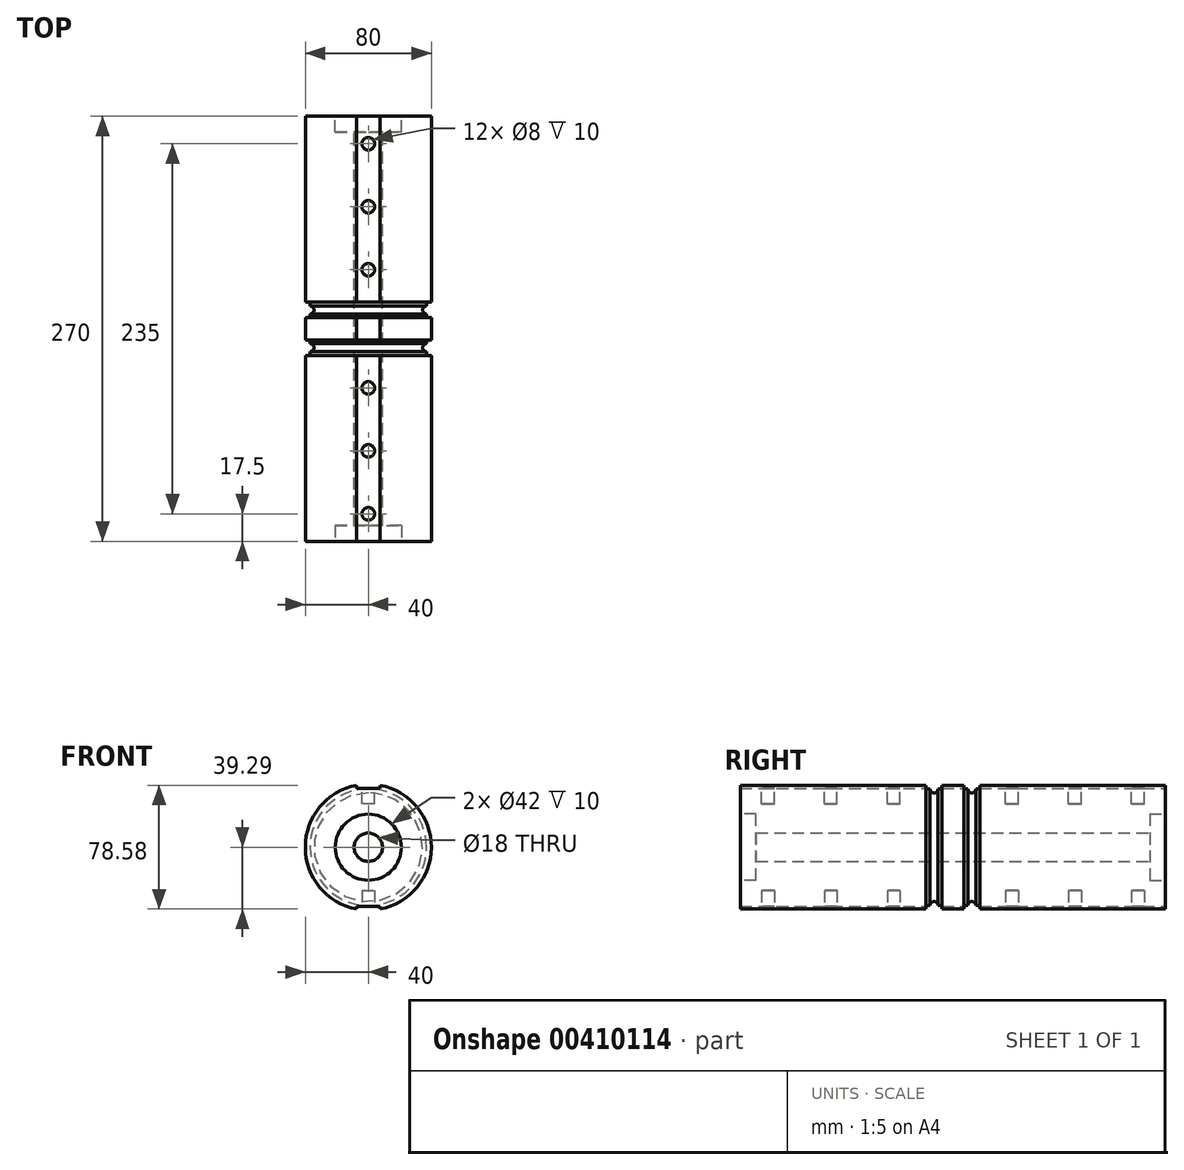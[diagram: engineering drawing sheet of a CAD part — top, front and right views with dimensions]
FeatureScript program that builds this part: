
annotation { "Feature Type Name" : "Feature", "Feature Type Description" : "" }
export const myFeature = defineFeature(function(context is Context, id is Id, definition is map)
    precondition{}
    {
        {
            var Q0;
            Q0=qCreatedBy(makeId("Front.planeOp"),FACE);
            var sketch = newSketch(context, id + "F0", { "sketchPlane" : qUnion([Q0])});
            skCircle(sketch, "E0", {"center": v(0, 0) * mm, "radius": 40 * mm});
            skCircle(sketch, "E1", {"center": v(0, 0) * mm, "radius": 9 * mm});
            skSolve(sketch);
        }
        {
            var Q0;
            Q0=qSketchRegion(id+"F0",true);
            extrude(context, id + "F1", {"entities" : qUnion([Q0]), "depth" : 270 * mm});
        }
        {
            var Q0;
            Q0=makeQuery(id+"F1.opExtrude","CAP_FACE",FACE,{"disambiguationData":[OSD([sQuery(id+"F0.wireOp",EDGE,"E0")])],"isStart":false});
            var sketch = newSketch(context, id + "F2", { "sketchPlane" : qUnion([Q0])});
            skSolve(sketch);
        }
        {
            var Q0;
            Q0=qCreatedBy(makeId("Front.planeOp"),FACE);
            var sketch = newSketch(context, id + "F3", { "sketchPlane" : qUnion([Q0])});
            skLineSegment(sketch, "E2.bottom", {"start": v(-7.5, 57.5) * mm, "end": v(7.5, 57.5) * mm});
            skLineSegment(sketch, "E2.top", {"start": v(-7.5, 37.5) * mm, "end": v(7.5, 37.5) * mm});
            skLineSegment(sketch, "E2.left", {"start": v(-7.5, 57.5) * mm, "end": v(-7.5, 37.5) * mm});
            skLineSegment(sketch, "E2.right", {"start": v(7.5, 57.5) * mm, "end": v(7.5, 37.5) * mm});
            skLineSegment(sketch, "E3.bottom", {"start": v(-7.5, -37.5) * mm, "end": v(7.5, -37.5) * mm});
            skLineSegment(sketch, "E3.top", {"start": v(-7.5, -57.5) * mm, "end": v(7.5, -57.5) * mm});
            skLineSegment(sketch, "E3.left", {"start": v(-7.5, -37.5) * mm, "end": v(-7.5, -57.5) * mm});
            skLineSegment(sketch, "E3.right", {"start": v(7.5, -37.5) * mm, "end": v(7.5, -57.5) * mm});
            skLineSegment(sketch, "E4", {"start": v(0, 37.5) * mm, "end": v(0, -37.5) * mm, "construction": true});
            skSolve(sketch);
        }
        {
            var Q0;
            Q0=qSketchRegion(id+"F3",true);
            var Q1;
            Q1=makeQuery(id+"F1.opExtrude","CAP_FACE",FACE,{"disambiguationData":[OSD([sQuery(id+"F0.wireOp",EDGE,"E0"),sQuery(id+"F0.wireOp",EDGE,"E1")])],"isStart":false});
            extrude(context, id + "F4", {"entities" : qUnion([Q0]), "operationType" : NewBodyOperationType.REMOVE, "endBound" : BoundingType.UP_TO_SURFACE, "endBoundEntityFace" : qUnion([Q1]), "depth" : 25 * mm});
        }
        {
            var Q0;
            Q0=makeQuery(id+"F2.imprint","IMPRINT",FACE,{"disambiguationData":[TD([[makeQuery(id+"F2.imprint","IMPRINT",EDGE,{"derivedFrom":makeQuery(id+"F1.opExtrude","CAP_EDGE",EDGE,{"disambiguationData":[OSD([sQuery(id+"F0.wireOp",EDGE,"E0")])],"isStart":false})}),1.0]])]});
            var sketch = newSketch(context, id + "F5", { "sketchPlane" : qUnion([Q0])});
            skCircle(sketch, "E5", {"center": v(0, 0) * mm, "radius": 21 * mm});
            skSolve(sketch);
        }
        {
            var Q0;
            Q0=qSketchRegion(id+"F5",true);
            extrude(context, id + "F6", {"entities" : qUnion([Q0]), "operationType" : NewBodyOperationType.REMOVE, "oppositeDirection" : true, "depth" : 10 * mm});
        }
        {
            var Q0;
            Q0=makeQuery(id+"F1.opExtrude","CAP_FACE",FACE,{"disambiguationData":[OSD([sQuery(id+"F0.wireOp",EDGE,"E0"),sQuery(id+"F0.wireOp",EDGE,"E1")])],"isStart":true});
            var sketch = newSketch(context, id + "F7", { "sketchPlane" : qUnion([Q0])});
            skCircle(sketch, "E6", {"center": v(0, 0) * mm, "radius": 21 * mm});
            skSolve(sketch);
        }
        {
            var Q0;
            Q0=qSketchRegion(id+"F7",true);
            extrude(context, id + "F8", {"entities" : qUnion([Q0]), "operationType" : NewBodyOperationType.REMOVE, "oppositeDirection" : true, "depth" : 10 * mm});
        }
        {
            var Q0;
            Q0=qCreatedBy(makeId("Right.planeOp"),FACE);
            var sketch = newSketch(context, id + "F9", { "sketchPlane" : qUnion([Q0])});
            skLineSegment(sketch, "E7", {"start": v(-135, 40) * mm, "end": v(-135, 0) * mm, "construction": true});
            skLineSegment(sketch, "E8.bottom", {"start": v(-118, 37) * mm, "end": v(-120.5, 37) * mm});
            skLineSegment(sketch, "E8.top", {"start": v(-118, 55.05) * mm, "end": v(-128, 55.05) * mm});
            skLineSegment(sketch, "E8.left", {"start": v(-118, 37) * mm, "end": v(-118, 55.05) * mm});
            skLineSegment(sketch, "E8.right", {"start": v(-128, 37) * mm, "end": v(-128, 55.05) * mm});
            skPoint(sketch, "E8.middle", {"position": v(-123, 46.03) * mm});
            skArc(sketch, "E9", {"start": v(-125.5, 37) * mm, "mid": v(-123, 34.5) * mm, "end": v(-120.5, 37) * mm});
            skLineSegment(sketch, "E10.bottom", {"start": v(-142, 37) * mm, "end": v(-144.5, 37) * mm});
            skLineSegment(sketch, "E10.top", {"start": v(-142, 54.07) * mm, "end": v(-152, 54.07) * mm});
            skLineSegment(sketch, "E10.left", {"start": v(-142, 37) * mm, "end": v(-142, 54.07) * mm});
            skLineSegment(sketch, "E10.right", {"start": v(-152, 37) * mm, "end": v(-152, 54.07) * mm});
            skPoint(sketch, "E10.middle", {"position": v(-147, 45.53) * mm});
            skArc(sketch, "E11", {"start": v(-149.5, 37) * mm, "mid": v(-147, 34.5) * mm, "end": v(-144.5, 37) * mm});
            skLineSegment(sketch, "E12.trimOffspring", {"start": v(-125.5, 37) * mm, "end": v(-128, 37) * mm});
            skLineSegment(sketch, "E13.trimOffspring", {"start": v(-149.5, 37) * mm, "end": v(-152, 37) * mm});
            skLineSegment(sketch, "E14", {"start": v(-270, 0) * mm, "end": v(0, 0) * mm});
            skLineSegment(sketch, "E15", {"start": v(-270, 40) * mm, "end": v(0, 40) * mm, "construction": true});
            skSolve(sketch);
        }
        {
            var Q0;
            Q0 = qSketchRegion(id + "F9", true);
            var Q1;
            Q1=sQuery(id+"F9.wireOp",EDGE,"E14");
            revolve(context, id + "F10", {"operationType" : NewBodyOperationType.REMOVE, "entities" : qUnion([Q0]), "axis" : qUnion([Q1]), "revolveType" : RevolveType.FULL, "oppositeDirection" : true});
        }
        {
            var Q0;
            Q0=makeQuery(id+"F10.boolean.opBoolean","SPLIT",FACE,{"disambiguationData":[TD([makeQuery(id+"F10.opRevolve","SWEPT_FACE",FACE,{"disambiguationData":[OSD([sQuery(id+"F9.wireOp",EDGE,"E8.left")])]})])],"derivedFrom":makeQuery(id+"F4.boolean.opBoolean","COPY",FACE,{"derivedFrom":makeQuery(id+"F4.opExtrude","SWEPT_FACE",FACE,{"disambiguationData":[OSD([sQuery(id+"F3.wireOp",EDGE,"E2.top")])]})})});
            var sketch = newSketch(context, id + "F11", { "sketchPlane" : qUnion([Q0])});
            skCircle(sketch, "E16", {"center": v(0, -17.5) * mm, "radius": 4 * mm});
            skCircle(sketch, "E17.0.1.0", {"center": v(0, -57.5) * mm, "radius": 4 * mm});
            skCircle(sketch, "E17.0.2.0", {"center": v(0, -97.5) * mm, "radius": 4 * mm});
            skLineSegment(sketch, "E17.direction1", {"start": v(0, -17.5) * mm, "end": v(25, -17.5) * mm, "construction": true});
            skLineSegment(sketch, "E17.direction2", {"start": v(0, -17.5) * mm, "end": v(0, -57.5) * mm, "construction": true});
            skCircle(sketch, "E18", {"center": v(0, -252.5) * mm, "radius": 4 * mm});
            skCircle(sketch, "E19.0.1.0", {"center": v(0, -212.5) * mm, "radius": 4 * mm});
            skCircle(sketch, "E19.0.2.0", {"center": v(0, -172.5) * mm, "radius": 4 * mm});
            skLineSegment(sketch, "E19.direction1", {"start": v(0, -252.5) * mm, "end": v(25, -252.5) * mm, "construction": true});
            skLineSegment(sketch, "E19.direction2", {"start": v(0, -252.5) * mm, "end": v(0, -212.5) * mm, "construction": true});
            skSolve(sketch);
        }
        {
            var Q0;
            Q0 = qSketchRegion(id + "F11", true);
            extrude(context, id + "F12", {"entities" : qUnion([Q0]), "operationType" : NewBodyOperationType.REMOVE, "oppositeDirection" : true, "depth" : 10 * mm});
        }
        {
            var Q0;
            Q0=makeQuery(id+"F10.boolean.opBoolean","SPLIT",FACE,{"disambiguationData":[TD([makeQuery(id+"F10.opRevolve","SWEPT_FACE",FACE,{"disambiguationData":[OSD([sQuery(id+"F9.wireOp",EDGE,"E10.right")])]})])],"derivedFrom":makeQuery(id+"F4.boolean.opBoolean","COPY",FACE,{"derivedFrom":makeQuery(id+"F4.opExtrude","SWEPT_FACE",FACE,{"disambiguationData":[OSD([sQuery(id+"F3.wireOp",EDGE,"E3.bottom")])]})})});
            var sketch = newSketch(context, id + "F13", { "sketchPlane" : qUnion([Q0])});
            skCircle(sketch, "E20.0", {"center": v(0, 17.5) * mm, "radius": 4 * mm});
            skCircle(sketch, "E20.1", {"center": v(0, 57.5) * mm, "radius": 4 * mm});
            skCircle(sketch, "E20.2", {"center": v(0, 97.5) * mm, "radius": 4 * mm});
            skLineSegment(sketch, "E20.3", {"start": v(0, 17.5) * mm, "end": v(25, 17.5) * mm});
            skLineSegment(sketch, "E20.4", {"start": v(0, 17.5) * mm, "end": v(0, 57.5) * mm});
            skCircle(sketch, "E20.5", {"center": v(0, 252.5) * mm, "radius": 4 * mm});
            skCircle(sketch, "E20.6", {"center": v(0, 212.5) * mm, "radius": 4 * mm});
            skCircle(sketch, "E20.7", {"center": v(0, 172.5) * mm, "radius": 4 * mm});
            skLineSegment(sketch, "E20.8", {"start": v(0, 252.5) * mm, "end": v(25, 252.5) * mm});
            skLineSegment(sketch, "E20.9", {"start": v(0, 252.5) * mm, "end": v(0, 212.5) * mm});
            skSolve(sketch);
        }
        {
            var Q0;
            Q0 = qSketchRegion(id + "F13", true);
            extrude(context, id + "F14", {"entities" : qUnion([Q0]), "operationType" : NewBodyOperationType.REMOVE, "oppositeDirection" : true, "depth" : 10 * mm});
        }
    });
